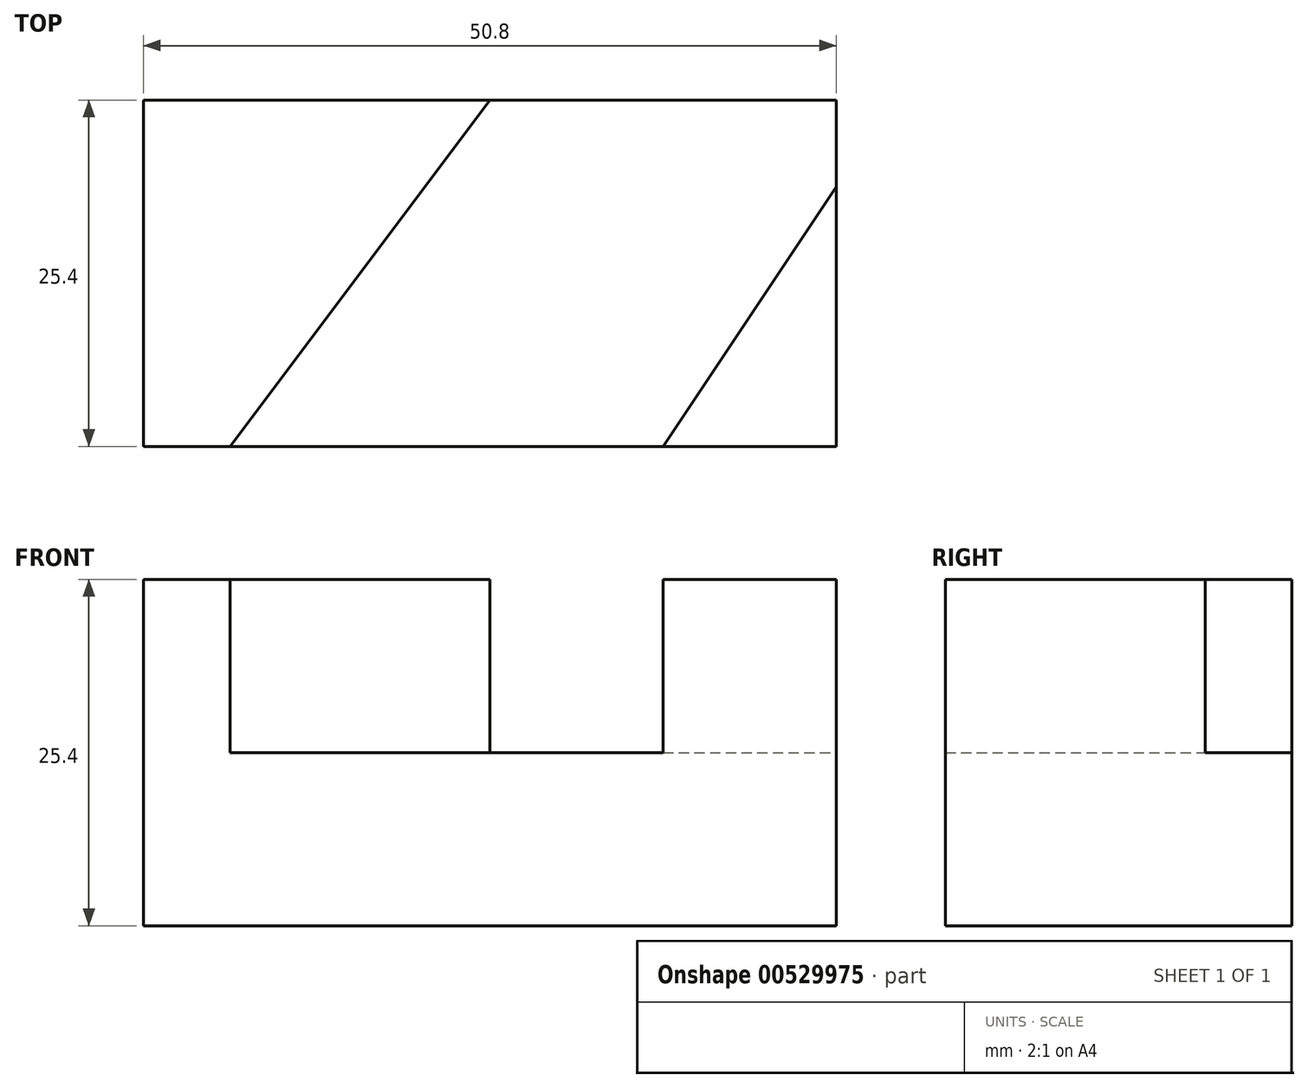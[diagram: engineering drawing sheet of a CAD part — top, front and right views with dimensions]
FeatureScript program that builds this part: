
annotation { "Feature Type Name" : "Feature", "Feature Type Description" : "" }
export const myFeature = defineFeature(function(context is Context, id is Id, definition is map)
    precondition{}
    {
        {
            var Q0;
            Q0=qCreatedBy(makeId("Top.planeOp"),FACE);
            var sketch = newSketch(context, id + "F0", { "sketchPlane" : qUnion([Q0])});
            skLineSegment(sketch, "E0", {"start": v(0, 25.4) * mm, "end": v(0, 0) * mm});
            skLineSegment(sketch, "E1", {"start": v(0, 0) * mm, "end": v(50.8, 0) * mm});
            skLineSegment(sketch, "E2", {"start": v(50.8, 0) * mm, "end": v(50.8, 25.4) * mm});
            skLineSegment(sketch, "E3", {"start": v(50.8, 25.4) * mm, "end": v(0, 25.4) * mm});
            skSolve(sketch);
        }
        {
            var Q0;
            Q0 = qSketchRegion(id + "F0", true);
            extrude(context, id + "F1", {"entities" : qUnion([Q0]), "depth" : 25.4 * mm, "offsetDistance" : 25.4 * mm});
        }
        {
            var Q0;
            Q0=makeQuery(id+"F1.opExtrude","CAP_FACE",FACE,{"disambiguationData":[OSD([sQuery(id+"F0.wireOp",EDGE,"E0"),sQuery(id+"F0.wireOp",EDGE,"E1"),sQuery(id+"F0.wireOp",EDGE,"E2"),sQuery(id+"F0.wireOp",EDGE,"E3")])],"isStart":false});
            var sketch = newSketch(context, id + "F2", { "sketchPlane" : qUnion([Q0])});
            skLineSegment(sketch, "E4", {"start": v(6.35, 0) * mm, "end": v(25.4, 25.4) * mm});
            skLineSegment(sketch, "E5", {"start": v(38.1, 0) * mm, "end": v(50.8, 19.05) * mm});
            skSolve(sketch);
        }
        {
            var Q0;
            Q0 = qSketchRegion(id + "F2", true);
            var Q1;
            {var subQ4=sQuery(id+"F2.wireOp",EDGE,"E4");Q1=makeQuery(id+"F2.imprint","IMPRINT",FACE,{"disambiguationData":[TD([[makeQuery(id+"F2.imprint","IMPRINT",EDGE,{"derivedFrom":subQ4}),-1.0]])]});}
            extrude(context, id + "F3", {"entities" : qUnion([Q0, Q1]), "operationType" : NewBodyOperationType.REMOVE, "oppositeDirection" : true, "depth" : 12.7 * mm, "offsetDistance" : 25.4 * mm});
        }
    });
